# Revit family: 5765210033(2020)
name_source: partatom
category: Plumbing Fixtures
revit_build: Autodesk Revit 2018 (Build: 20170223_1515(x64)
units: mm (PartAtom-declared; Revit-internal decimal feet)

## family parameters
Always vertical = Yes
Cut with Voids When Loaded = No
OmniClass Number = 23.45.55.00
OmniClass Title = Sanitary Faucets, Wastes
Part Type = Normal
Room Calculation Point = No
Round Connector Dimension = Use Diameter
Shared = No
Work Plane-Based = No

## types (1)
- 5765210033 Spout, L=197
    2D/3D/BIM Files URL = http://static.hansa.com
    3D View = https://static.hansa.com
    Advanced Features = Inner body made of DZR brass
    Aerator = Hidden aerator
    Ambience photo = http://static.hansa.com
    AssetType = Fixed
    BIMObjectName = 5765210033(2020)
    BodyMaterial = Brass
    Brand = HANSA
    Catalog Drawing URL = http://static.hansa.com
    Category = Bathroom
    CloseOffRating = 0
    Color = Chrome
    Concealed Parts = Square rosette;Round rosette
    Connection Size = G1/2
    Dimension Drawing URL = http://static.hansa.com
    DurationUnit = Year
    EAN Number = 4057304015717
    ETIM Class Number = EC011421 Outlet for sanitary taps
    FDV Document URL = http://www.hansa.com
    FaucetMainMaterial = Brass
    Finish = Polished
    FlowCoefficient = 0
    Group = Spout
    IfcExportAs = IfcValveType
    IfcExportType = FAUCET
    Installation Type = Wall mounted
    Installation and Maintenance Guide URL = http://static.hansa.com
    Interactive AR View URL = https://static.hansa.com
    Manufacturer = HANSA
    ManufacturerName = HANSA
    ManufacturerURL = http://www.hansa.com
    Market = Germany;Austria;Belgium;Netherlands
    Material = Brass
    Mobile Product Information URL = http://mpi.hansa.com
    Model = 5765210033 Spout, L=197
    ModelReference = 5765210033
    NBSDescription = Water supply fittings for wash basins and troughs
    NBSReference = 45-35-70/371
    Name = 5765210033 Spout, L=197
    Name_en = 5765210033 Spout, L=197
    NominalDepth = 217 mm  [stored 0.711942 ft]
    NominalHeight = 75 mm  [stored 0.246063 ft]
    NominalWidth = 75 mm  [stored 0.246063 ft]
    Product Code = 5765210033
    Product Family = HANSALOFT
    Product Image URL = http://static.hansa.com
    Product URL = http://static.hansa.com
    Revision = 2
    Sales Package dimensions (LxWxH) = 240 x 85 x 66
    Shape = Sculptured
    Size = 75 x 215 x75 mm
    Spare-Part Information URL = http://static.hansa.com
    Spout Projection = 197 mm
    Spout Type = Fixed spout;Casted construction
    Surface treatment = Matt black
    Technical DataSheet URL = http://www.hansa.com
    UNSPSC Class Number = 30181807 Spout
    URL REACH = http://static.hansa.com
    Uniclass2 = Pr_40_30_96_97
    Uniclass2015Description = Washbasin spouts
    Uniclass2015Reference = Pr_40_20_87_97
    Version = 2
    VersionDate = 01/07/2022
    Warranty Information URL = http://warranty.hansa.com
    WarrantyDescription = http://warranty.hansa.com
    WarrantyDurationUnit = Year

note: [stored X ft] marks values corroborated as IEEE doubles in the binary element streams (Revit-internal decimal feet)

## geometry (parser evidence)
native form markers: Sweep x4
no freeform markers — native parametric forms only
